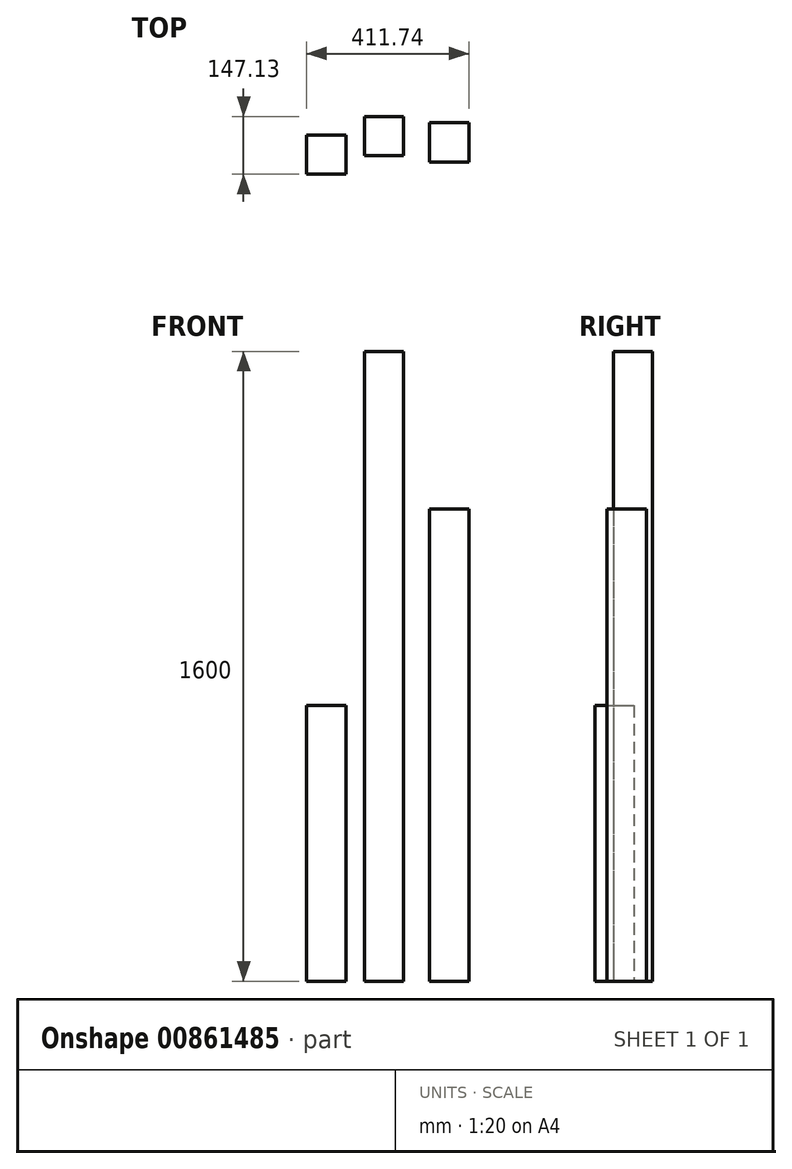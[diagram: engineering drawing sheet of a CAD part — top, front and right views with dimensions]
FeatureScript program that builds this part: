
annotation { "Feature Type Name" : "Feature", "Feature Type Description" : "" }
export const myFeature = defineFeature(function(context is Context, id is Id, definition is map)
    precondition{}
    {
        {
            var Q0;
            Q0=qCreatedBy(makeId("Top.planeOp"),FACE);
            var sketch = newSketch(context, id + "F0", { "sketchPlane" : qUnion([Q0])});
            skLineSegment(sketch, "E0.bottom", {"start": v(-184.45, 142.91) * mm, "end": v(-284.45, 142.91) * mm});
            skLineSegment(sketch, "E0.top", {"start": v(-184.45, 242.91) * mm, "end": v(-284.45, 242.91) * mm});
            skLineSegment(sketch, "E0.left", {"start": v(-184.45, 142.91) * mm, "end": v(-184.45, 242.91) * mm});
            skLineSegment(sketch, "E0.right", {"start": v(-284.45, 142.91) * mm, "end": v(-284.45, 242.91) * mm});
            skPoint(sketch, "E0.middle", {"position": v(-234.45, 192.91) * mm});
            skLineSegment(sketch, "E1.bottom", {"start": v(-38.3, 190.04) * mm, "end": v(-138.3, 190.04) * mm});
            skLineSegment(sketch, "E1.top", {"start": v(-38.3, 290.04) * mm, "end": v(-138.3, 290.04) * mm});
            skLineSegment(sketch, "E1.left", {"start": v(-38.3, 190.04) * mm, "end": v(-38.3, 290.04) * mm});
            skLineSegment(sketch, "E1.right", {"start": v(-138.3, 190.04) * mm, "end": v(-138.3, 290.04) * mm});
            skPoint(sketch, "E1.middle", {"position": v(-88.3, 240.04) * mm});
            skLineSegment(sketch, "E2.bottom", {"start": v(27.29, 173.68) * mm, "end": v(127.29, 173.68) * mm});
            skLineSegment(sketch, "E2.top", {"start": v(27.29, 273.68) * mm, "end": v(127.29, 273.68) * mm});
            skLineSegment(sketch, "E2.left", {"start": v(27.29, 173.68) * mm, "end": v(27.29, 273.68) * mm});
            skLineSegment(sketch, "E2.right", {"start": v(127.29, 173.68) * mm, "end": v(127.29, 273.68) * mm});
            skPoint(sketch, "E2.middle", {"position": v(77.29, 223.68) * mm});
            skLineSegment(sketch, "E3.bottom", {"start": v(223.24, 133.58) * mm, "end": v(323.24, 133.58) * mm});
            skLineSegment(sketch, "E3.top", {"start": v(223.24, 233.58) * mm, "end": v(323.24, 233.58) * mm});
            skLineSegment(sketch, "E3.left", {"start": v(223.24, 133.58) * mm, "end": v(223.24, 233.58) * mm});
            skLineSegment(sketch, "E3.right", {"start": v(323.24, 133.58) * mm, "end": v(323.24, 233.58) * mm});
            skPoint(sketch, "E3.middle", {"position": v(273.24, 183.58) * mm});
            skLineSegment(sketch, "E4.bottom", {"start": v(-50, -134.53) * mm, "end": v(50, -134.53) * mm});
            skLineSegment(sketch, "E4.top", {"start": v(-50, -34.53) * mm, "end": v(50, -34.53) * mm});
            skLineSegment(sketch, "E4.left", {"start": v(-50, -134.53) * mm, "end": v(-50, -34.53) * mm});
            skLineSegment(sketch, "E4.right", {"start": v(50, -134.53) * mm, "end": v(50, -34.53) * mm});
            skPoint(sketch, "E4.middle", {"position": v(0, -84.53) * mm});
            skSolve(sketch);
        }
        {
            var Q0;
            Q0=makeQuery(id+"F0.imprint","IMPRINT",FACE,{"disambiguationData":[TD([[makeQuery(id+"F0.imprint","IMPRINT",EDGE,{"derivedFrom":sQuery(id+"F0.wireOp",EDGE,"E0.bottom")}),-1.0]])]});
            extrude(context, id + "F1", {"entities" : qUnion([Q0]), "depth" : 700 * mm, "offsetDistance" : 25 * mm});
        }
        {
            var Q0;
            Q0=makeQuery(id+"F0.imprint","IMPRINT",FACE,{"disambiguationData":[TD([[makeQuery(id+"F0.imprint","IMPRINT",EDGE,{"derivedFrom":sQuery(id+"F0.wireOp",EDGE,"E1.bottom")}),-1.0]])]});
            extrude(context, id + "F2", {"entities" : qUnion([Q0]), "depth" : 1600 * mm, "offsetDistance" : 25 * mm});
        }
        {
            var Q0;
            Q0=makeQuery(id+"F0.imprint","IMPRINT",FACE,{"disambiguationData":[TD([[makeQuery(id+"F0.imprint","IMPRINT",EDGE,{"derivedFrom":sQuery(id+"F0.wireOp",EDGE,"E2.bottom")}),1.0]])]});
            extrude(context, id + "F3", {"entities" : qUnion([Q0]), "depth" : 1200 * mm, "offsetDistance" : 25 * mm});
        }
    });
